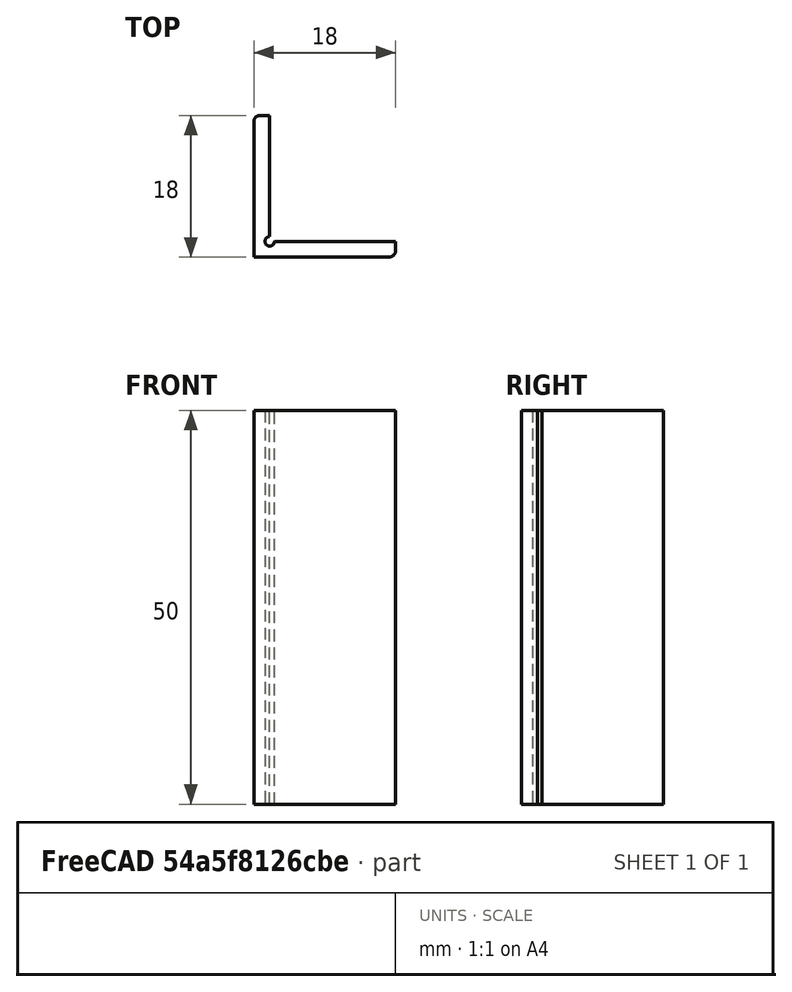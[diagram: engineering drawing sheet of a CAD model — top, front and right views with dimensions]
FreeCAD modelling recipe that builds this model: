
FCSTD DOCUMENT  (FreeCAD 0.22R36958 (Git))
Label: corner protector
License: All rights reserved
LicenseURL: http://en.wikipedia.org/wiki/All_rights_reserved
objects: Sketcher::SketchObject×1, PartDesign::Pad×1, PartDesign::Body×1
note: 4 computed .brp shape members not serialized (recipe doc carries the construction recipe); baked Part::Feature solids carry a one-line shape summary decoded from their .brp

FEATURE [Sketcher::SketchObject] Sketch
  AttachmentSupport = -> [XY_Plane]
  FullyConstrained = true
  MapMode = 5
  sketch-geometry (11):
    g0: LineSegment StartX=7e-16 StartY=17.2 StartZ=0 EndX=7e-16 EndY=0 EndZ=0
    g1: LineSegment StartX=7e-16 StartY=0 StartZ=0 EndX=17.2 EndY=0 EndZ=0
    g2: LineSegment StartX=18 StartY=0.8 StartZ=0 EndX=18 EndY=2 EndZ=0
    g3: LineSegment StartX=18 StartY=2 StartZ=0 EndX=2.6 EndY=2 EndZ=0
    g4: LineSegment StartX=2 StartY=2.6 StartZ=0 EndX=2 EndY=18 EndZ=0
    g5: LineSegment StartX=2 StartY=18 StartZ=0 EndX=0.8 EndY=18 EndZ=0
    g6: ArcOfCircle CenterX=2 CenterY=2 CenterZ=0 NormalX=0 NormalY=0 NormalZ=1 AngleXU=0 Radius=0.6 StartAngle=1.5708 EndAngle=6.28319
    g7: ArcOfCircle CenterX=0.8 CenterY=17.2 CenterZ=0 NormalX=0 NormalY=0 NormalZ=1 AngleXU=0 Radius=0.8 StartAngle=1.5708 EndAngle=3.14159
    g8: GeomPoint X=0 Y=18 Z=0
    g9: ArcOfCircle CenterX=17.2 CenterY=0.8 CenterZ=0 NormalX=0 NormalY=0 NormalZ=1 AngleXU=0 Radius=0.8 StartAngle=4.71239 EndAngle=6.28319
    g10: GeomPoint X=18 Y=0 Z=0
  constraints (29):
    c: Vertical(g0)
    c: Coincident(g0,g1)
    c: Horizontal(g1)
    c: Coincident(g2,g3)
    c: Horizontal(g3)
    c: Vertical(g4)
    c: Coincident(g4,g5)
    c: Horizontal(g5)
    c: DistanceX(g8,g5) = 2
    c: Vertical(g2)
    c: DistanceY(g10,g2) = 2
    c: DistanceY(g0,g8) = 18
    c: DistanceX(g1,g10) = 18
    c: Coincident(g3,g6)
    c: Coincident(g4,g6)
    c: Radius(g6) = 0.6
    c: Perpendicular(g6,g3)
    c: Perpendicular(g6,g4)
    c: Coincident(g0,g-1)
    c: PointOnObject(g8,g5)
    c: PointOnObject(g8,g0)
    c: Tangent(g5,g7) = -1.5708
    c: Tangent(g0,g7) = -1.5708
    c: PointOnObject(g10,g1)
    c: PointOnObject(g10,g2)
    c: Tangent(g1,g9) = -1.5708
    c: Tangent(g2,g9) = -1.5708
    c: Radius(g9) = 0.8
    c: Equal(g9,g7)
FEATURE [PartDesign::Pad] Pad
  Direction = (0,0,1)
  Length = 50
  Length2 = 10
  Profile = -> Sketch
  ReferenceAxis = -> Sketch [N_Axis]
  Suppressed = false
  Type = 0
FEATURE [PartDesign::Body] Body
  Group = -> [Sketch,Pad]
  Origin = -> Origin
  Tip = -> Pad
